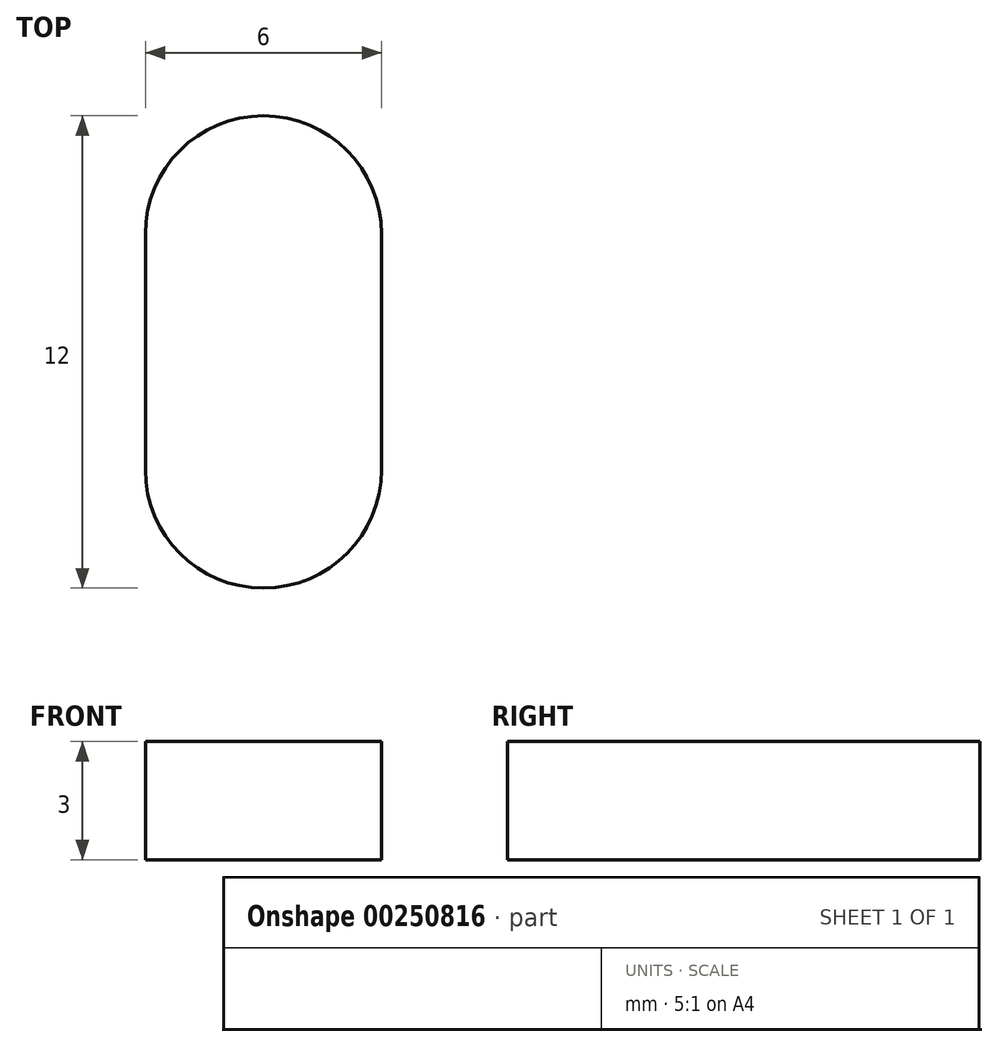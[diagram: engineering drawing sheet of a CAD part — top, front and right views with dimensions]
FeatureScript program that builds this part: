
annotation { "Feature Type Name" : "Feature", "Feature Type Description" : "" }
export const myFeature = defineFeature(function(context is Context, id is Id, definition is map)
    precondition{}
    {
        {
            var Q0;
            Q0=qCreatedBy(makeId("Top.planeOp"),FACE);
            var sketch = newSketch(context, id + "F0", { "sketchPlane" : qUnion([Q0])});
            skLineSegment(sketch, "E0", {"start": v(0, -3) * mm, "end": v(0, 3) * mm});
            skArc(sketch, "E1.0.startCap", {"start": v(3, -3) * mm, "mid": v(0, -6) * mm, "end": v(-3, -3) * mm});
            skArc(sketch, "E1.0.endCap", {"start": v(-3, 3) * mm, "mid": v(0, 6) * mm, "end": v(3, 3) * mm});
            skLineSegment(sketch, "E1.0.left", {"start": v(-3, -3) * mm, "end": v(-3, 3) * mm});
            skLineSegment(sketch, "E1.0.right", {"start": v(3, -3) * mm, "end": v(3, 3) * mm});
            skSolve(sketch);
        }
        {
            var Q0;
            Q0 = qSketchRegion(id + "F0", true);
            extrude(context, id + "F1", {"entities" : qUnion([Q0]), "depth" : 3 * mm, "offsetDistance" : 25 * mm});
        }
    });
